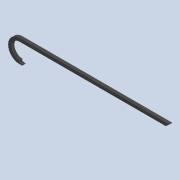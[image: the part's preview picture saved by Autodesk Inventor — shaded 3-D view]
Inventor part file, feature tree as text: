
AUTODESK INVENTOR PART (.ipt)
format: ipt  version: 2020 (Build 240168000, 168)  size: 155,648 bytes
history: native  units: mm
features: sketch x3, plane x1, sweep x1, extrude x1
ambient origin geometry x8: Origin, YZ Plane, XZ Plane, XY Plane, X Axis, Y Axis, Z Axis, Center Point
bodies: Solid1 (feature_tree)
feature tree (6):
  sketch  "Sketch1"  dims[d0=500.0mm d1=69.0mm]
  plane  "Work Plane1"
  sweep  "Sweep1"
  extrude  "Extrusion1"  Depth=7.0mm
  sketch  "Sketch2"  dims[d2=7.0mm d3=7.0mm]
  sketch  "Sketch3"  dims[d4=2.0mm d5=0.0mm d6=0.0mm d11=0.0mm d12=0.0mm d25=10.0mm d29=17.453293mm d30=10.0mm d33=17.453293mm d34=10.0mm]
